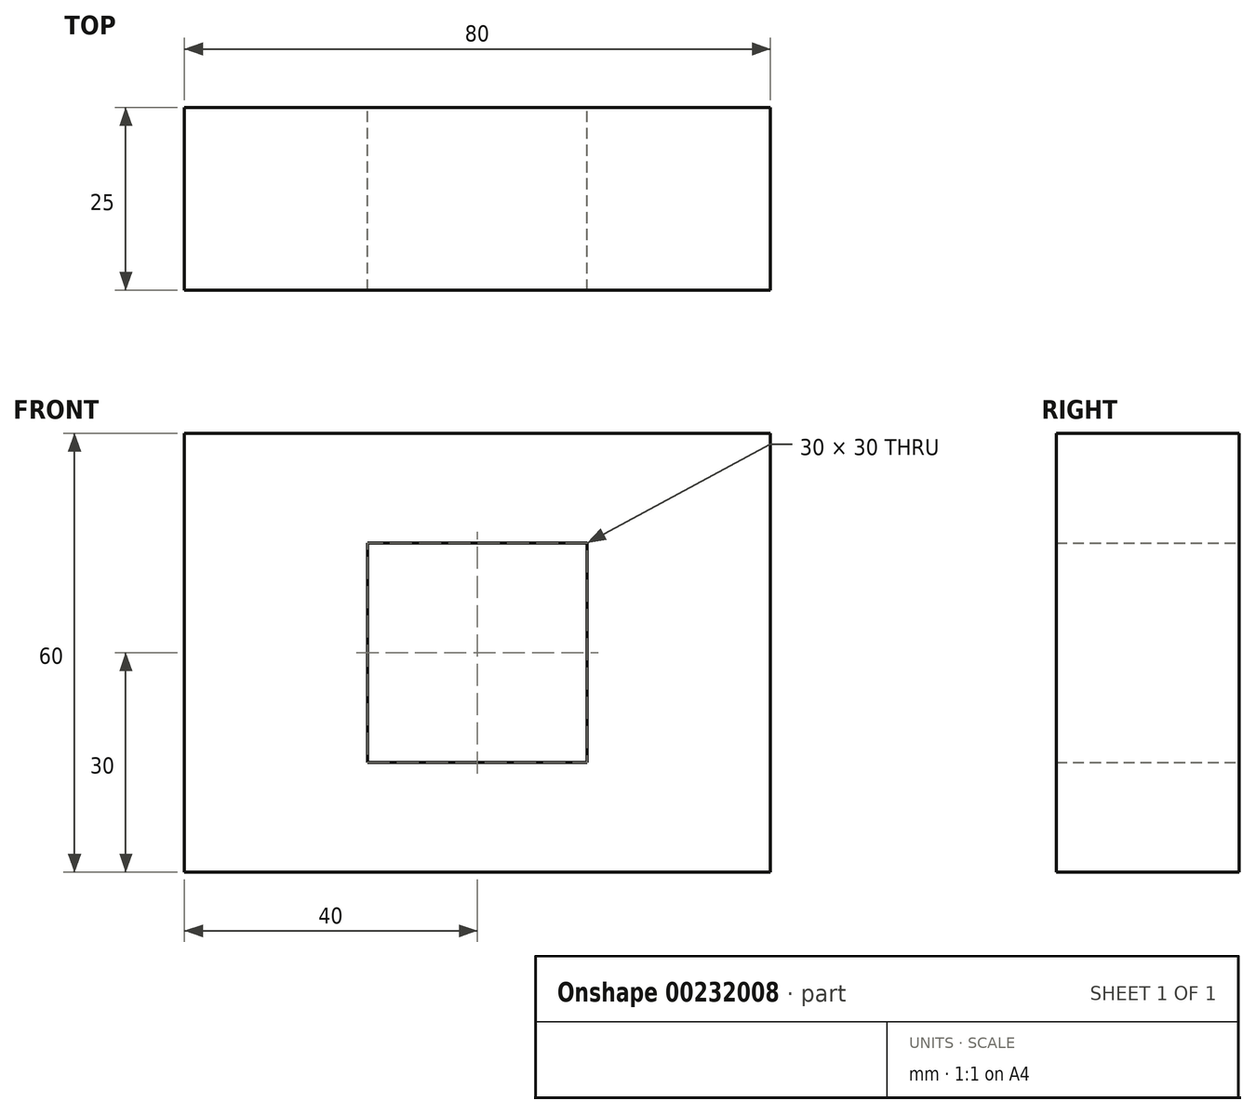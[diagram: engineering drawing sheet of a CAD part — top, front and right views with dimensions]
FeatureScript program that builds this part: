
annotation { "Feature Type Name" : "Feature", "Feature Type Description" : "" }
export const myFeature = defineFeature(function(context is Context, id is Id, definition is map)
    precondition{}
    {
        {
            var Q0;
            Q0=qCreatedBy(makeId("Front.planeOp"),FACE);
            var sketch = newSketch(context, id + "F0", { "sketchPlane" : qUnion([Q0])});
            skLineSegment(sketch, "E0.bottom", {"start": v(0, 30) * mm, "end": v(30, 30) * mm});
            skLineSegment(sketch, "E0.top", {"start": v(0, 0) * mm, "end": v(30, 0) * mm});
            skLineSegment(sketch, "E0.left", {"start": v(0, 30) * mm, "end": v(0, 0) * mm});
            skLineSegment(sketch, "E0.right", {"start": v(30, 30) * mm, "end": v(30, 0) * mm});
            skLineSegment(sketch, "E1.bottom", {"start": v(-25, 45) * mm, "end": v(55, 45) * mm});
            skLineSegment(sketch, "E1.top", {"start": v(-25, -15) * mm, "end": v(55, -15) * mm});
            skLineSegment(sketch, "E1.left", {"start": v(-25, 45) * mm, "end": v(-25, -15) * mm});
            skLineSegment(sketch, "E1.right", {"start": v(55, 45) * mm, "end": v(55, -15) * mm});
            skSolve(sketch);
        }
        {
            var Q0;
            Q0=makeQuery(id+"F0.imprint","IMPRINT",FACE,{"disambiguationData":[TD([[makeQuery(id+"F0.imprint","IMPRINT",EDGE,{"derivedFrom":sQuery(id+"F0.wireOp",EDGE,"E0.bottom")}),1.0]])]});
            extrude(context, id + "F1", {"entities" : qUnion([Q0]), "depth" : 25 * mm});
        }
    });
